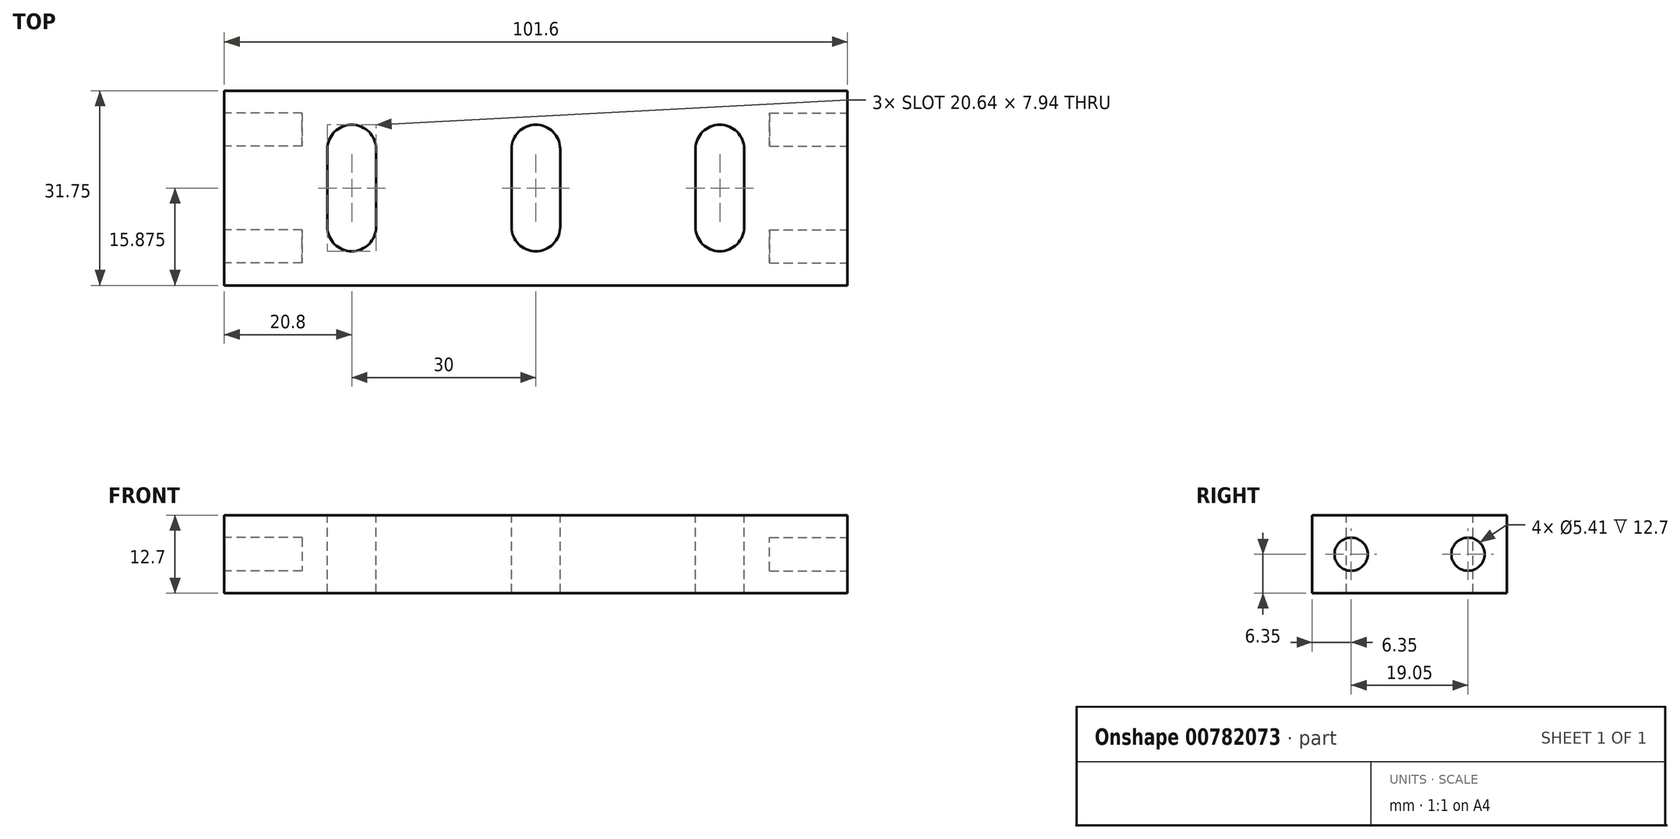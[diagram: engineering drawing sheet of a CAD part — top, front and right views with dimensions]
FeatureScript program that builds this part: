
annotation { "Feature Type Name" : "Feature", "Feature Type Description" : "" }
export const myFeature = defineFeature(function(context is Context, id is Id, definition is map)
    precondition{}
    {
        {
            var Q0;
            Q0=qCreatedBy(makeId("Top.planeOp"),FACE);
            var sketch = newSketch(context, id + "F0", { "sketchPlane" : qUnion([Q0])});
            skLineSegment(sketch, "E0.bottom", {"start": v(0, 0) * mm, "end": v(101.6, 0) * mm});
            skLineSegment(sketch, "E0.top", {"start": v(0, 31.75) * mm, "end": v(101.6, 31.75) * mm});
            skLineSegment(sketch, "E0.left", {"start": v(0, 0) * mm, "end": v(0, 31.75) * mm});
            skLineSegment(sketch, "E0.right", {"start": v(101.6, 0) * mm, "end": v(101.6, 31.75) * mm});
            skSolve(sketch);
        }
        {
            var Q0;
            Q0 = qSketchRegion(id + "F0", true);
            extrude(context, id + "F1", {"entities" : qUnion([Q0]), "depth" : 12.7 * mm, "offsetDistance" : 25.4 * mm});
        }
        {
            var Q0;
            Q0=makeQuery(id+"F1.opExtrude","CAP_FACE",FACE,{"disambiguationData":[OSD([sQuery(id+"F0.wireOp",EDGE,"E0.bottom"),sQuery(id+"F0.wireOp",EDGE,"E0.top"),sQuery(id+"F0.wireOp",EDGE,"E0.left"),sQuery(id+"F0.wireOp",EDGE,"E0.right")])],"isStart":false});
            var sketch = newSketch(context, id + "F2", { "sketchPlane" : qUnion([Q0])});
            skLineSegment(sketch, "E1", {"start": v(50.8, 31.75) * mm, "end": v(50.8, 0) * mm, "construction": true});
            skLineSegment(sketch, "E2", {"start": v(16.83, 22.23) * mm, "end": v(16.83, 9.53) * mm});
            skLineSegment(sketch, "E3", {"start": v(24.77, 22.23) * mm, "end": v(24.77, 9.53) * mm});
            skArc(sketch, "E4", {"start": v(16.83, 22.23) * mm, "mid": v(20.8, 26.2) * mm, "end": v(24.77, 22.23) * mm});
            skArc(sketch, "E5", {"start": v(24.77, 9.52) * mm, "mid": v(20.8, 5.56) * mm, "end": v(16.83, 9.53) * mm});
            skLineSegment(sketch, "E6.MirrorCS", {"start": v(76.83, 22.23) * mm, "end": v(76.83, 9.53) * mm});
            skLineSegment(sketch, "E7.MirrorCS", {"start": v(84.77, 22.23) * mm, "end": v(84.77, 9.53) * mm});
            skArc(sketch, "E8.MirrorCS", {"start": v(84.77, 22.23) * mm, "mid": v(80.8, 26.2) * mm, "end": v(76.83, 22.23) * mm});
            skArc(sketch, "E9.MirrorCS", {"start": v(76.83, 9.53) * mm, "mid": v(80.8, 5.56) * mm, "end": v(84.77, 9.53) * mm});
            skLineSegment(sketch, "E10", {"start": v(46.83, 22.23) * mm, "end": v(46.83, 9.53) * mm});
            skLineSegment(sketch, "E11", {"start": v(54.77, 22.23) * mm, "end": v(54.77, 9.53) * mm});
            skArc(sketch, "E12", {"start": v(46.83, 22.23) * mm, "mid": v(50.8, 26.2) * mm, "end": v(54.77, 22.23) * mm});
            skArc(sketch, "E13", {"start": v(54.77, 9.53) * mm, "mid": v(50.8, 5.56) * mm, "end": v(46.83, 9.53) * mm});
            skLineSegment(sketch, "E14", {"start": v(0, 15.88) * mm, "end": v(101.6, 15.88) * mm, "construction": true});
            skSolve(sketch);
        }
        {
            var Q0;
            Q0 = qSketchRegion(id + "F2", true);
            extrude(context, id + "F3", {"entities" : qUnion([Q0]), "operationType" : NewBodyOperationType.REMOVE, "oppositeDirection" : true, "depth" : 25.4 * mm, "offsetDistance" : 25.4 * mm});
        }
        {
            var Q0;
            Q0=makeQuery(id+"F1.opExtrude","SWEPT_FACE",FACE,{"disambiguationData":[OSD([sQuery(id+"F0.wireOp",EDGE,"E0.right")])]});
            var sketch = newSketch(context, id + "F4", { "sketchPlane" : qUnion([Q0])});
            skCircle(sketch, "E15", {"center": v(6.35, 6.35) * mm, "radius": 2.7 * mm});
            skCircle(sketch, "E16", {"center": v(25.4, 6.35) * mm, "radius": 2.7 * mm});
            skSolve(sketch);
        }
        {
            var Q0;
            Q0 = qSketchRegion(id + "F4", true);
            extrude(context, id + "F5", {"entities" : qUnion([Q0]), "operationType" : NewBodyOperationType.REMOVE, "oppositeDirection" : true, "depth" : 12.7 * mm, "offsetDistance" : 25.4 * mm});
        }
        {
            var Q0;
            Q0=makeQuery(id+"F1.opExtrude","SWEPT_FACE",FACE,{"disambiguationData":[OSD([sQuery(id+"F0.wireOp",EDGE,"E0.left")])]});
            var sketch = newSketch(context, id + "F6", { "sketchPlane" : qUnion([Q0])});
            skCircle(sketch, "E17", {"center": v(-25.4, 6.35) * mm, "radius": 2.7 * mm});
            skCircle(sketch, "E18", {"center": v(-6.35, 6.35) * mm, "radius": 2.7 * mm});
            skSolve(sketch);
        }
        {
            var Q0;
            Q0 = qSketchRegion(id + "F6", true);
            extrude(context, id + "F7", {"entities" : qUnion([Q0]), "operationType" : NewBodyOperationType.REMOVE, "oppositeDirection" : true, "depth" : 12.7 * mm, "offsetDistance" : 25.4 * mm});
        }
    });
